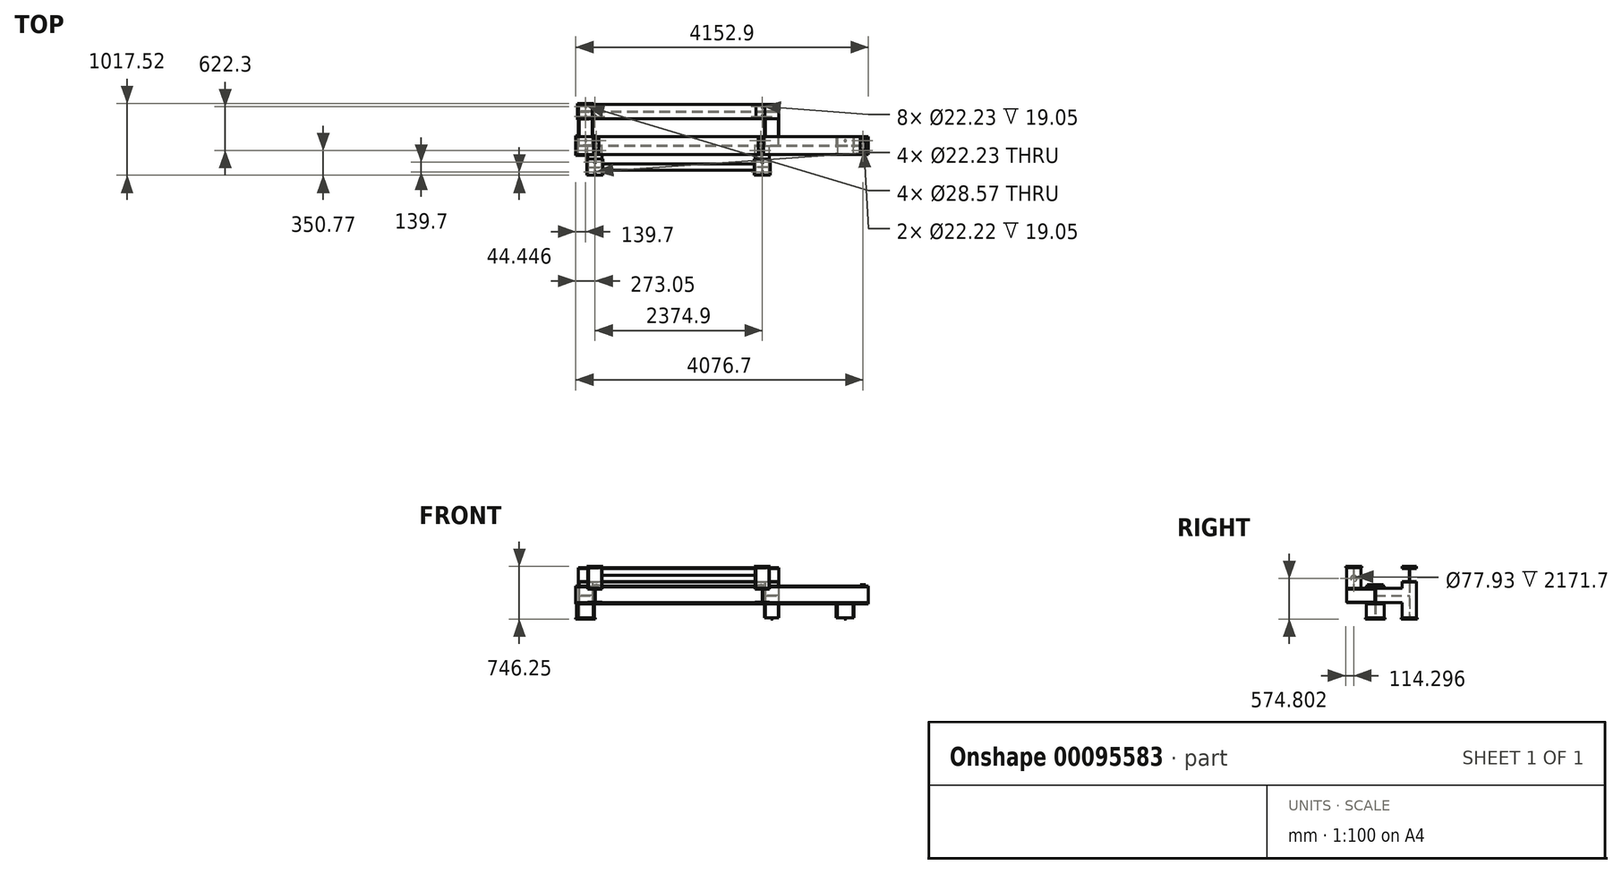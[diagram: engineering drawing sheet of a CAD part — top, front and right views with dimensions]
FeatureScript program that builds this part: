
annotation { "Feature Type Name" : "Feature", "Feature Type Description" : "" }
export const myFeature = defineFeature(function(context is Context, id is Id, definition is map)
    precondition{}
    {
        {
            var Q0;
            Q0=qCreatedBy(makeId("Top.planeOp"),FACE);
            var sketch = newSketch(context, id + "F0", { "sketchPlane" : qUnion([Q0])});
            skLineSegment(sketch, "E0.bottom", {"start": v(-1320.8, 241.3) * mm, "end": v(1320.8, 241.3) * mm, "construction": true});
            skLineSegment(sketch, "E0.top", {"start": v(-1320.8, -241.3) * mm, "end": v(1320.8, -241.3) * mm, "construction": true});
            skLineSegment(sketch, "E0.left", {"start": v(-1320.8, 241.3) * mm, "end": v(-1320.8, -241.3) * mm, "construction": true});
            skLineSegment(sketch, "E0.right", {"start": v(1320.8, 241.3) * mm, "end": v(1320.8, -241.3) * mm, "construction": true});
            skPoint(sketch, "E0.middle", {"position": v(0, 0) * mm});
            skLineSegment(sketch, "E1.bottom", {"start": v(-1435.1, 355.6) * mm, "end": v(-1206.5, 355.6) * mm});
            skLineSegment(sketch, "E1.top", {"start": v(-1435.1, 127) * mm, "end": v(-1206.5, 127) * mm});
            skLineSegment(sketch, "E1.left", {"start": v(-1435.1, 355.6) * mm, "end": v(-1435.1, 127) * mm});
            skLineSegment(sketch, "E1.right", {"start": v(-1206.5, 355.6) * mm, "end": v(-1206.5, 127) * mm});
            skPoint(sketch, "E1.middle", {"position": v(-1320.8, 241.3) * mm});
            skLineSegment(sketch, "E2", {"start": v(0, -413.23) * mm, "end": v(0, 639.03) * mm, "construction": true});
            skLineSegment(sketch, "E3", {"start": v(-1320.8, 355.6) * mm, "end": v(-1320.8, 127) * mm, "construction": true});
            skLineSegment(sketch, "E4", {"start": v(-1435.1, 241.3) * mm, "end": v(-1206.5, 241.3) * mm, "construction": true});
            skLineSegment(sketch, "E5.0", {"start": v(-1435.1, 311.15) * mm, "end": v(-1206.5, 311.15) * mm, "construction": true});
            skCircle(sketch, "E6", {"center": v(-1320.8, 311.15) * mm, "radius": 14.29 * mm});
            skCircle(sketch, "E7.MirrorC", {"center": v(-1320.8, 171.45) * mm, "radius": 14.29 * mm});
            skCircle(sketch, "E8.MirrorC", {"center": v(1320.8, 311.15) * mm, "radius": 14.29 * mm});
            skCircle(sketch, "E9.MirrorC", {"center": v(1320.8, 171.45) * mm, "radius": 14.29 * mm});
            skLineSegment(sketch, "E10.MirrorCS", {"start": v(1435.1, 311.15) * mm, "end": v(1206.5, 311.15) * mm, "construction": true});
            skLineSegment(sketch, "E11.MirrorCS", {"start": v(1435.1, 241.3) * mm, "end": v(1206.5, 241.3) * mm, "construction": true});
            skLineSegment(sketch, "E12.MirrorCS", {"start": v(1320.8, 355.6) * mm, "end": v(1320.8, 127) * mm, "construction": true});
            skLineSegment(sketch, "E13.MirrorCS", {"start": v(1435.1, 355.6) * mm, "end": v(1206.5, 355.6) * mm});
            skPoint(sketch, "E14.MirrorP", {"position": v(1320.8, 241.3) * mm});
            skLineSegment(sketch, "E15.MirrorCS", {"start": v(1206.5, 355.6) * mm, "end": v(1206.5, 127) * mm});
            skLineSegment(sketch, "E16.MirrorCS", {"start": v(1435.1, 127) * mm, "end": v(1206.5, 127) * mm});
            skLineSegment(sketch, "E17.MirrorCS", {"start": v(1435.1, 355.6) * mm, "end": v(1435.1, 127) * mm});
            skLineSegment(sketch, "E18.bottom", {"start": v(-1460.5, -381) * mm, "end": v(-1181.1, -381) * mm});
            skLineSegment(sketch, "E18.top", {"start": v(-1460.5, -101.6) * mm, "end": v(-1181.1, -101.6) * mm});
            skLineSegment(sketch, "E18.left", {"start": v(-1460.5, -381) * mm, "end": v(-1460.5, -101.6) * mm});
            skLineSegment(sketch, "E18.right", {"start": v(-1181.1, -381) * mm, "end": v(-1181.1, -101.6) * mm});
            skPoint(sketch, "E18.middle", {"position": v(-1320.8, -241.3) * mm});
            skLineSegment(sketch, "E19", {"start": v(-1320.8, -241.3) * mm, "end": v(-1460.5, -241.3) * mm, "construction": true});
            skLineSegment(sketch, "E20.0", {"start": v(-1320.8, -171.45) * mm, "end": v(-1460.5, -171.45) * mm, "construction": true});
            skCircle(sketch, "E21", {"center": v(-1320.8, -171.45) * mm, "radius": 14.29 * mm});
            skCircle(sketch, "E22.MirrorC", {"center": v(-1320.8, -311.15) * mm, "radius": 14.29 * mm});
            skLineSegment(sketch, "E23", {"start": v(-1320.8, -638.8) * mm, "end": v(-1320.8, -1011) * mm, "construction": true});
            skPoint(sketch, "E24.orphan", {"position": v(-1320.8, -381) * mm});
            skLineSegment(sketch, "E25.0", {"start": v(0, -638.8) * mm, "end": v(0, -1011) * mm, "construction": true});
            skLineSegment(sketch, "E26.0", {"start": v(1320.8, -638.8) * mm, "end": v(1320.8, -1011) * mm, "construction": true});
            skLineSegment(sketch, "E27.0", {"start": v(2362.2, -638.8) * mm, "end": v(2362.2, -1011) * mm, "construction": true});
            skLineSegment(sketch, "E28", {"start": v(-1320.8, -1011) * mm, "end": v(2362.2, -1011) * mm, "construction": true});
            skLineSegment(sketch, "E29", {"start": v(520.7, -1011) * mm, "end": v(520.7, -1354.57) * mm, "construction": true});
            skCircle(sketch, "E30.MirrorC", {"center": v(2362.2, -171.45) * mm, "radius": 14.29 * mm});
            skCircle(sketch, "E31.MirrorC", {"center": v(2362.2, -311.15) * mm, "radius": 14.29 * mm});
            skLineSegment(sketch, "E32.MirrorCS", {"start": v(2362.2, -171.45) * mm, "end": v(2501.9, -171.45) * mm, "construction": true});
            skLineSegment(sketch, "E33.MirrorCS", {"start": v(2501.9, -101.6) * mm, "end": v(2222.5, -101.6) * mm});
            skLineSegment(sketch, "E34.MirrorCS", {"start": v(2501.9, -381) * mm, "end": v(2222.5, -381) * mm});
            skLineSegment(sketch, "E35.MirrorCS", {"start": v(2362.2, -241.3) * mm, "end": v(2501.9, -241.3) * mm, "construction": true});
            skPoint(sketch, "E36.MirrorP", {"position": v(2362.2, -241.3) * mm});
            skLineSegment(sketch, "E37.MirrorCS", {"start": v(2222.5, -381) * mm, "end": v(2222.5, -101.6) * mm});
            skPoint(sketch, "E38.MirrorP", {"position": v(2362.2, -381) * mm});
            skLineSegment(sketch, "E39.MirrorCS", {"start": v(2501.9, -381) * mm, "end": v(2501.9, -101.6) * mm});
            skSolve(sketch);
        }
        {
            var Q0;
            Q0=makeQuery(id+"F0.imprint","IMPRINT",FACE,{"disambiguationData":[TD([[makeQuery(id+"F0.imprint","IMPRINT",EDGE,{"derivedFrom":sQuery(id+"F0.wireOp",EDGE,"E1.bottom")}),-1.0]])]});
            var Q1;
            Q1=makeQuery(id+"F0.imprint","IMPRINT",FACE,{"disambiguationData":[TD([[makeQuery(id+"F0.imprint","IMPRINT",EDGE,{"derivedFrom":sQuery(id+"F0.wireOp",EDGE,"E8.MirrorC")}),1.0]])]});
            var Q2;
            Q2=makeQuery(id+"F0.imprint","IMPRINT",FACE,{"disambiguationData":[TD([[makeQuery(id+"F0.imprint","IMPRINT",EDGE,{"derivedFrom":sQuery(id+"F0.wireOp",EDGE,"E30.MirrorC")}),1.0]])]});
            var Q3;
            Q3=makeQuery(id+"F0.imprint","IMPRINT",FACE,{"disambiguationData":[TD([[makeQuery(id+"F0.imprint","IMPRINT",EDGE,{"derivedFrom":sQuery(id+"F0.wireOp",EDGE,"E18.bottom")}),1.0]])]});
            extrude(context, id + "F1", {"entities" : qUnion([Q0, Q1, Q2, Q3]), "depth" : 19.05 * mm});
        }
        {
            var Q0;
            Q0=makeQuery(id+"F1.opExtrude","CAP_FACE",FACE,{"disambiguationData":[OSD([sQuery(id+"F0.wireOp",EDGE,"E1.bottom"),sQuery(id+"F0.wireOp",EDGE,"E1.top"),sQuery(id+"F0.wireOp",EDGE,"E1.left"),sQuery(id+"F0.wireOp",EDGE,"E1.right"),sQuery(id+"F0.wireOp",EDGE,"E6"),sQuery(id+"F0.wireOp",EDGE,"E7.MirrorC")])],"isStart":false});
            var sketch = newSketch(context, id + "F2", { "sketchPlane" : qUnion([Q0])});
            skLineSegment(sketch, "E40.0", {"start": v(-1435.1, 241.3) * mm, "end": v(-1206.5, 241.3) * mm, "construction": true});
            skLineSegment(sketch, "E41.0", {"start": v(-1320.8, 355.6) * mm, "end": v(-1320.8, 127) * mm, "construction": true});
            skLineSegment(sketch, "E42.bottom", {"start": v(-1422.4, 342.9) * mm, "end": v(-1411.35, 342.9) * mm});
            skLineSegment(sketch, "E42.top", {"start": v(-1422.4, 139.7) * mm, "end": v(-1411.35, 139.7) * mm});
            skLineSegment(sketch, "E42.left", {"start": v(-1422.4, 342.9) * mm, "end": v(-1422.4, 139.7) * mm});
            skLineSegment(sketch, "E42.right", {"start": v(-1219.2, 342.9) * mm, "end": v(-1219.2, 139.7) * mm, "construction": true});
            skPoint(sketch, "E42.middle", {"position": v(-1320.8, 241.3) * mm});
            skLineSegment(sketch, "E43.0", {"start": v(-1411.35, 342.9) * mm, "end": v(-1411.35, 251.27) * mm});
            skLineSegment(sketch, "E44.trimOffspring", {"start": v(-1405, 237.68) * mm, "end": v(-1320.8, 237.68) * mm});
            skLineSegment(sketch, "E45.MirrorCS", {"start": v(-1405, 244.92) * mm, "end": v(-1320.8, 244.92) * mm});
            skLineSegment(sketch, "E46.trimOffspring", {"start": v(-1411.35, 231.33) * mm, "end": v(-1411.35, 139.7) * mm});
            skPoint(sketch, "E47.visualSharp", {"position": v(-1411.35, 244.92) * mm});
            skArc(sketch, "E47.filletArc", {"start": v(-1411.35, 251.27) * mm, "mid": v(-1409.5, 246.78) * mm, "end": v(-1405, 244.92) * mm});
            skPoint(sketch, "E48.visualSharp", {"position": v(-1411.35, 237.68) * mm});
            skArc(sketch, "E48.filletArc", {"start": v(-1405, 237.68) * mm, "mid": v(-1409.5, 235.82) * mm, "end": v(-1411.35, 231.33) * mm});
            skArc(sketch, "E49.MirrorCS", {"start": v(-1236.6, 237.68) * mm, "mid": v(-1232.1, 235.82) * mm, "end": v(-1230.25, 231.33) * mm});
            skArc(sketch, "E50.MirrorCS", {"start": v(-1230.25, 251.27) * mm, "mid": v(-1232.1, 246.78) * mm, "end": v(-1236.6, 244.92) * mm});
            skPoint(sketch, "E51.MirrorP", {"position": v(-1230.25, 237.68) * mm});
            skPoint(sketch, "E52.MirrorP", {"position": v(-1230.25, 244.92) * mm});
            skLineSegment(sketch, "E53.MirrorCS", {"start": v(-1230.25, 342.9) * mm, "end": v(-1230.25, 251.27) * mm});
            skLineSegment(sketch, "E54.MirrorCS", {"start": v(-1236.6, 237.68) * mm, "end": v(-1320.8, 237.68) * mm});
            skLineSegment(sketch, "E55.MirrorCS", {"start": v(-1236.6, 244.92) * mm, "end": v(-1320.8, 244.92) * mm});
            skLineSegment(sketch, "E56.MirrorCS", {"start": v(-1219.2, 139.7) * mm, "end": v(-1230.25, 139.7) * mm});
            skLineSegment(sketch, "E57.MirrorCS", {"start": v(-1230.25, 231.33) * mm, "end": v(-1230.25, 139.7) * mm});
            skLineSegment(sketch, "E58.MirrorCS", {"start": v(-1219.2, 342.9) * mm, "end": v(-1230.25, 342.9) * mm});
            skLineSegment(sketch, "E59.MirrorCS", {"start": v(-1219.2, 342.9) * mm, "end": v(-1219.2, 139.7) * mm});
            skLineSegment(sketch, "E60.0", {"start": v(0, -413.23) * mm, "end": v(0, 639.03) * mm, "construction": true});
            skArc(sketch, "E61.MirrorCS", {"start": v(1411.35, 251.27) * mm, "mid": v(1409.5, 246.78) * mm, "end": v(1405, 244.92) * mm});
            skArc(sketch, "E62.MirrorCS", {"start": v(1405, 237.68) * mm, "mid": v(1409.5, 235.82) * mm, "end": v(1411.35, 231.33) * mm});
            skLineSegment(sketch, "E63.MirrorCS", {"start": v(1236.6, 244.92) * mm, "end": v(1320.8, 244.92) * mm});
            skArc(sketch, "E64.MirrorCS", {"start": v(1236.6, 237.68) * mm, "mid": v(1232.1, 235.82) * mm, "end": v(1230.25, 231.33) * mm});
            skLineSegment(sketch, "E65.MirrorCS", {"start": v(1422.4, 139.7) * mm, "end": v(1411.35, 139.7) * mm});
            skLineSegment(sketch, "E66.MirrorCS", {"start": v(1422.4, 342.9) * mm, "end": v(1411.35, 342.9) * mm});
            skArc(sketch, "E67.MirrorCS", {"start": v(1230.25, 251.27) * mm, "mid": v(1232.1, 246.78) * mm, "end": v(1236.6, 244.92) * mm});
            skLineSegment(sketch, "E68.MirrorCS", {"start": v(1236.6, 237.68) * mm, "end": v(1320.8, 237.68) * mm});
            skLineSegment(sketch, "E69.MirrorCS", {"start": v(1435.1, 241.3) * mm, "end": v(1206.5, 241.3) * mm, "construction": true});
            skLineSegment(sketch, "E70.MirrorCS", {"start": v(1405, 237.68) * mm, "end": v(1320.8, 237.68) * mm});
            skLineSegment(sketch, "E71.MirrorCS", {"start": v(1219.2, 342.9) * mm, "end": v(1230.25, 342.9) * mm});
            skLineSegment(sketch, "E72.MirrorCS", {"start": v(1219.2, 139.7) * mm, "end": v(1230.25, 139.7) * mm});
            skLineSegment(sketch, "E73.MirrorCS", {"start": v(1411.35, 342.9) * mm, "end": v(1411.35, 251.27) * mm});
            skLineSegment(sketch, "E74.MirrorCS", {"start": v(1405, 244.92) * mm, "end": v(1320.8, 244.92) * mm});
            skLineSegment(sketch, "E75.MirrorCS", {"start": v(1411.35, 231.33) * mm, "end": v(1411.35, 139.7) * mm});
            skPoint(sketch, "E76.MirrorP", {"position": v(1411.35, 237.68) * mm});
            skPoint(sketch, "E77.MirrorP", {"position": v(1320.8, 241.3) * mm});
            skLineSegment(sketch, "E78.MirrorCS", {"start": v(1219.2, 342.9) * mm, "end": v(1219.2, 139.7) * mm, "construction": true});
            skLineSegment(sketch, "E79.MirrorCS", {"start": v(1422.4, 342.9) * mm, "end": v(1422.4, 139.7) * mm});
            skPoint(sketch, "E80.MirrorP", {"position": v(1230.25, 237.68) * mm});
            skLineSegment(sketch, "E81.MirrorCS", {"start": v(1320.8, 355.6) * mm, "end": v(1320.8, 127) * mm, "construction": true});
            skPoint(sketch, "E82.MirrorP", {"position": v(1411.35, 244.92) * mm});
            skLineSegment(sketch, "E83.MirrorCS", {"start": v(1219.2, 342.9) * mm, "end": v(1219.2, 139.7) * mm});
            skLineSegment(sketch, "E84.MirrorCS", {"start": v(1230.25, 231.33) * mm, "end": v(1230.25, 139.7) * mm});
            skLineSegment(sketch, "E85.MirrorCS", {"start": v(1230.25, 342.9) * mm, "end": v(1230.25, 251.27) * mm});
            skPoint(sketch, "E86.MirrorP", {"position": v(1230.25, 244.92) * mm});
            skSolve(sketch);
        }
        {
            var Q0;
            Q0 = qSketchRegion(id + "F2", true);
            extrude(context, id + "F3", {"entities" : qUnion([Q0]), "depth" : 504.95 * mm});
        }
        {
            var Q0;
            Q0=makeQuery(id+"F3.opExtrude","SWEPT_FACE",FACE,{"disambiguationData":[OSD([sQuery(id+"F2.wireOp",EDGE,"E79.MirrorCS")])]});
            var sketch = newSketch(context, id + "F4", { "sketchPlane" : qUnion([Q0])});
            skLineSegment(sketch, "E87.bottom", {"start": v(139.7, 524) * mm, "end": v(342.9, 524) * mm});
            skLineSegment(sketch, "E87.top", {"start": v(139.7, 727.2) * mm, "end": v(342.9, 727.2) * mm});
            skLineSegment(sketch, "E87.left", {"start": v(139.7, 524) * mm, "end": v(139.7, 535.05) * mm});
            skLineSegment(sketch, "E87.right", {"start": v(342.9, 524) * mm, "end": v(342.9, 535.05) * mm});
            skLineSegment(sketch, "E88", {"start": v(241.3, 727.2) * mm, "end": v(241.3, 524) * mm, "construction": true});
            skLineSegment(sketch, "E89.0", {"start": v(237.68, 709.8) * mm, "end": v(237.68, 541.4) * mm});
            skLineSegment(sketch, "E90.MirrorCS", {"start": v(244.92, 709.8) * mm, "end": v(244.92, 541.4) * mm});
            skLineSegment(sketch, "E91.0", {"start": v(139.7, 716.15) * mm, "end": v(231.33, 716.15) * mm});
            skLineSegment(sketch, "E92.0", {"start": v(139.7, 535.05) * mm, "end": v(231.33, 535.05) * mm});
            skLineSegment(sketch, "E93.trimOffspring", {"start": v(251.27, 716.15) * mm, "end": v(342.9, 716.15) * mm});
            skLineSegment(sketch, "E94.trimOffspring", {"start": v(251.27, 535.05) * mm, "end": v(342.9, 535.05) * mm});
            skLineSegment(sketch, "E95.trimOffspring", {"start": v(139.7, 716.15) * mm, "end": v(139.7, 727.2) * mm});
            skLineSegment(sketch, "E96.trimOffspring", {"start": v(342.9, 716.15) * mm, "end": v(342.9, 727.2) * mm});
            skPoint(sketch, "E97.newPointB", {"position": v(237.68, 524) * mm});
            skArc(sketch, "E97.filletArc", {"start": v(231.33, 535.05) * mm, "mid": v(235.82, 536.91) * mm, "end": v(237.68, 541.4) * mm});
            skPoint(sketch, "E98.newPointA", {"position": v(244.92, 524) * mm});
            skArc(sketch, "E98.filletArc", {"start": v(244.92, 541.4) * mm, "mid": v(246.78, 536.91) * mm, "end": v(251.27, 535.05) * mm});
            skPoint(sketch, "E99.newPointA", {"position": v(237.68, 727.2) * mm});
            skArc(sketch, "E99.filletArc", {"start": v(237.68, 709.8) * mm, "mid": v(235.82, 714.3) * mm, "end": v(231.33, 716.15) * mm});
            skPoint(sketch, "E100.newPointA", {"position": v(244.92, 727.2) * mm});
            skArc(sketch, "E100.filletArc", {"start": v(251.27, 716.15) * mm, "mid": v(246.78, 714.3) * mm, "end": v(244.92, 709.8) * mm});
            skSolve(sketch);
        }
        {
            var Q0;
            Q0 = qSketchRegion(id + "F4", true);
            var Q1;
            Q1=makeQuery(id+"F3.opExtrude","SWEPT_FACE",FACE,{"disambiguationData":[OSD([sQuery(id+"F2.wireOp",EDGE,"E42.left")])]});
            extrude(context, id + "F5", {"entities" : qUnion([Q0]), "endBound" : BoundingType.UP_TO_SURFACE, "oppositeDirection" : true, "endBoundEntityFace" : qUnion([Q1]), "depth" : 25.4 * mm});
        }
        {
            var Q0;
            Q0=makeQuery(id+"F5.opExtrude","SWEPT_FACE",FACE,{"disambiguationData":[OSD([sQuery(id+"F4.wireOp",EDGE,"E87.top")])]});
            var sketch = newSketch(context, id + "F6", { "sketchPlane" : qUnion([Q0])});
            skLineSegment(sketch, "E101.0", {"start": v(0, -413.23) * mm, "end": v(0, 639.03) * mm, "construction": true});
            skLineSegment(sketch, "E102.0", {"start": v(-1187.45, -413.23) * mm, "end": v(-1187.45, 639.03) * mm, "construction": true});
            skLineSegment(sketch, "E103.0", {"start": v(-1225.55, 139.7) * mm, "end": v(-1225.55, 342.9) * mm});
            skLineSegment(sketch, "E104.0", {"start": v(-1098.55, 139.7) * mm, "end": v(-1098.55, 342.9) * mm});
            skLineSegment(sketch, "E105.0", {"start": v(-1422.4, 342.9) * mm, "end": v(1422.4, 342.9) * mm, "construction": true});
            skLineSegment(sketch, "E106.0.0", {"start": v(1225.55, 342.9) * mm, "end": v(-1225.55, 342.9) * mm});
            skLineSegment(sketch, "E106.0.1", {"start": v(-1422.4, 342.9) * mm, "end": v(-1422.4, 139.7) * mm});
            skLineSegment(sketch, "E106.0.2", {"start": v(-1225.55, 139.7) * mm, "end": v(-1098.55, 139.7) * mm});
            skLineSegment(sketch, "E106.0.3", {"start": v(1422.4, 139.7) * mm, "end": v(1422.4, 342.9) * mm});
            skLineSegment(sketch, "E107.trimOffspring", {"start": v(0, 139.7) * mm, "end": v(1225.55, 139.7) * mm});
            skLineSegment(sketch, "E108.0", {"start": v(-1320.8, 241.3) * mm, "end": v(1320.8, 241.3) * mm, "construction": true});
            skLineSegment(sketch, "E109.0", {"start": v(-1320.8, 311.15) * mm, "end": v(1320.8, 311.15) * mm, "construction": true});
            skCircle(sketch, "E110", {"center": v(-1187.45, 311.15) * mm, "radius": 11.11 * mm});
            skCircle(sketch, "E111.MirrorC", {"center": v(-1187.45, 171.45) * mm, "radius": 11.11 * mm});
            skCircle(sketch, "E112.MirrorC", {"center": v(1187.45, 311.15) * mm, "radius": 11.11 * mm});
            skCircle(sketch, "E113.MirrorC", {"center": v(1187.45, 171.45) * mm, "radius": 11.11 * mm});
            skLineSegment(sketch, "E114.MirrorCS", {"start": v(1225.55, 139.7) * mm, "end": v(1098.55, 139.7) * mm});
            skLineSegment(sketch, "E115.MirrorCS", {"start": v(1225.55, 139.7) * mm, "end": v(1225.55, 342.9) * mm});
            skLineSegment(sketch, "E116.MirrorCS", {"start": v(1098.55, 139.7) * mm, "end": v(1098.55, 342.9) * mm});
            skSolve(sketch);
        }
        {
            var Q0;
            Q0 = qSketchRegion(id + "F6", true);
            extrude(context, id + "F7", {"entities" : qUnion([Q0]), "operationType" : NewBodyOperationType.ADD, "depth" : 19.05 * mm});
        }
        {
            var Q0;
            Q0=makeQuery(id+"F3.opExtrude","SWEPT_FACE",FACE,{"disambiguationData":[OSD([sQuery(id+"F2.wireOp",EDGE,"E44.trimOffspring"),sQuery(id+"F2.wireOp",EDGE,"E54.MirrorCS")])]});
            var sketch = newSketch(context, id + "F8", { "sketchPlane" : qUnion([Q0])});
            skLineSegment(sketch, "E117.0", {"start": v(-1460.5, 0) * mm, "end": v(-1181.1, 0) * mm, "construction": true});
            skLineSegment(sketch, "E118", {"start": v(-1320.8, 0) * mm, "end": v(-1320.8, 868.41) * mm, "construction": true});
            skLineSegment(sketch, "E119.0", {"start": v(-1422.4, 231.65) * mm, "end": v(-1411.35, 231.65) * mm});
            skLineSegment(sketch, "E120.0", {"start": v(-1422.4, 434.85) * mm, "end": v(-1411.35, 434.85) * mm});
            skLineSegment(sketch, "E121", {"start": v(-1422.4, 434.85) * mm, "end": v(-1422.4, 231.65) * mm});
            skLineSegment(sketch, "E122.0", {"start": v(-1411.35, 434.85) * mm, "end": v(-1411.35, 342.77) * mm});
            skLineSegment(sketch, "E123", {"start": v(-1411.35, 333.25) * mm, "end": v(-1320.8, 333.25) * mm, "construction": true});
            skLineSegment(sketch, "E124.0", {"start": v(-1405, 336.42) * mm, "end": v(-1320.8, 336.42) * mm});
            skLineSegment(sketch, "E125.MirrorCS", {"start": v(-1410.08, 330.07) * mm, "end": v(-1320.8, 330.07) * mm});
            skLineSegment(sketch, "E126.trimOffspring", {"start": v(-1411.35, 328.8) * mm, "end": v(-1411.35, 231.65) * mm});
            skPoint(sketch, "E127.newPointA", {"position": v(-1411.35, 336.42) * mm});
            skArc(sketch, "E127.filletArc", {"start": v(-1411.35, 342.77) * mm, "mid": v(-1409.5, 338.28) * mm, "end": v(-1405, 336.42) * mm});
            skPoint(sketch, "E128.visualSharp", {"position": v(-1411.35, 330.07) * mm});
            skArc(sketch, "E128.filletArc", {"start": v(-1410.08, 330.07) * mm, "mid": v(-1410.98, 329.7) * mm, "end": v(-1411.35, 328.8) * mm});
            skArc(sketch, "E129.MirrorCS", {"start": v(-1231.52, 330.07) * mm, "mid": v(-1230.62, 329.7) * mm, "end": v(-1230.25, 328.8) * mm});
            skArc(sketch, "E130.MirrorCS", {"start": v(-1230.25, 342.77) * mm, "mid": v(-1232.1, 338.28) * mm, "end": v(-1236.6, 336.42) * mm});
            skLineSegment(sketch, "E131.MirrorCS", {"start": v(-1219.2, 231.65) * mm, "end": v(-1230.25, 231.65) * mm});
            skLineSegment(sketch, "E132.MirrorCS", {"start": v(-1219.2, 434.85) * mm, "end": v(-1230.25, 434.85) * mm});
            skPoint(sketch, "E133.MirrorP", {"position": v(-1230.25, 336.42) * mm});
            skPoint(sketch, "E134.MirrorP", {"position": v(-1230.25, 330.07) * mm});
            skLineSegment(sketch, "E135.MirrorCS", {"start": v(-1230.25, 328.8) * mm, "end": v(-1230.25, 231.65) * mm});
            skLineSegment(sketch, "E136.MirrorCS", {"start": v(-1231.52, 330.07) * mm, "end": v(-1320.8, 330.07) * mm});
            skLineSegment(sketch, "E137.MirrorCS", {"start": v(-1219.2, 434.85) * mm, "end": v(-1219.2, 231.65) * mm});
            skLineSegment(sketch, "E138.MirrorCS", {"start": v(-1230.25, 434.85) * mm, "end": v(-1230.25, 342.77) * mm});
            skLineSegment(sketch, "E139.MirrorCS", {"start": v(-1230.25, 333.25) * mm, "end": v(-1320.8, 333.25) * mm, "construction": true});
            skLineSegment(sketch, "E140.MirrorCS", {"start": v(-1236.6, 336.42) * mm, "end": v(-1320.8, 336.42) * mm});
            skLineSegment(sketch, "E141", {"start": v(0, -179.83) * mm, "end": v(0, 965.66) * mm, "construction": true});
            skArc(sketch, "E142.MirrorCS", {"start": v(1411.35, 342.77) * mm, "mid": v(1409.5, 338.28) * mm, "end": v(1405, 336.42) * mm});
            skArc(sketch, "E143.MirrorCS", {"start": v(1410.08, 330.07) * mm, "mid": v(1410.98, 329.7) * mm, "end": v(1411.35, 328.8) * mm});
            skArc(sketch, "E144.MirrorCS", {"start": v(1230.25, 342.77) * mm, "mid": v(1232.1, 338.28) * mm, "end": v(1236.6, 336.42) * mm});
            skArc(sketch, "E145.MirrorCS", {"start": v(1231.52, 330.07) * mm, "mid": v(1230.62, 329.7) * mm, "end": v(1230.25, 328.8) * mm});
            skLineSegment(sketch, "E146.MirrorCS", {"start": v(1411.35, 333.25) * mm, "end": v(1320.8, 333.25) * mm, "construction": true});
            skLineSegment(sketch, "E147.MirrorCS", {"start": v(1219.2, 231.65) * mm, "end": v(1230.25, 231.65) * mm});
            skLineSegment(sketch, "E148.MirrorCS", {"start": v(1219.2, 434.85) * mm, "end": v(1230.25, 434.85) * mm});
            skLineSegment(sketch, "E149.MirrorCS", {"start": v(1422.4, 231.65) * mm, "end": v(1411.35, 231.65) * mm});
            skLineSegment(sketch, "E150.MirrorCS", {"start": v(1422.4, 434.85) * mm, "end": v(1411.35, 434.85) * mm});
            skLineSegment(sketch, "E151.MirrorCS", {"start": v(1405, 336.42) * mm, "end": v(1320.8, 336.42) * mm});
            skLineSegment(sketch, "E152.MirrorCS", {"start": v(1410.08, 330.07) * mm, "end": v(1320.8, 330.07) * mm});
            skLineSegment(sketch, "E153.MirrorCS", {"start": v(1230.25, 333.25) * mm, "end": v(1320.8, 333.25) * mm, "construction": true});
            skLineSegment(sketch, "E154.MirrorCS", {"start": v(1231.52, 330.07) * mm, "end": v(1320.8, 330.07) * mm});
            skLineSegment(sketch, "E155.MirrorCS", {"start": v(1236.6, 336.42) * mm, "end": v(1320.8, 336.42) * mm});
            skLineSegment(sketch, "E156.MirrorCS", {"start": v(1411.35, 328.8) * mm, "end": v(1411.35, 231.65) * mm});
            skPoint(sketch, "E157.MirrorP", {"position": v(1411.35, 330.07) * mm});
            skPoint(sketch, "E158.MirrorP", {"position": v(1411.35, 336.42) * mm});
            skLineSegment(sketch, "E159.MirrorCS", {"start": v(1422.4, 434.85) * mm, "end": v(1422.4, 231.65) * mm});
            skLineSegment(sketch, "E160.MirrorCS", {"start": v(1411.35, 434.85) * mm, "end": v(1411.35, 342.77) * mm});
            skLineSegment(sketch, "E161.MirrorCS", {"start": v(1230.25, 434.85) * mm, "end": v(1230.25, 342.77) * mm});
            skLineSegment(sketch, "E162.MirrorCS", {"start": v(1230.25, 328.8) * mm, "end": v(1230.25, 231.65) * mm});
            skPoint(sketch, "E163.MirrorP", {"position": v(1230.25, 330.07) * mm});
            skPoint(sketch, "E164.MirrorP", {"position": v(1230.25, 336.42) * mm});
            skLineSegment(sketch, "E165.MirrorCS", {"start": v(1219.2, 434.85) * mm, "end": v(1219.2, 231.65) * mm});
            skSolve(sketch);
        }
        {
            var Q0;
            Q0 = qSketchRegion(id + "F8", true);
            extrude(context, id + "F9", {"entities" : qUnion([Q0]), "operationType" : NewBodyOperationType.ADD, "depth" : 482.6 * mm});
        }
        {
            var Q0;
            Q0=qCreatedBy(makeId("Right.planeOp"),FACE);
            cPlane(context, id + "F10", {"entities" : qUnion([Q0]), "cplaneType" : CPlaneType.OFFSET, "offset" : 2692.4 * mm, "width" : 152.4 * mm, "height" : 152.4 * mm});
        }
        {
            var Q0;
            Q0=qCreatedBy(id+"F10.planeOp",FACE);
            var sketch = newSketch(context, id + "F11", { "sketchPlane" : qUnion([Q0])});
            skLineSegment(sketch, "E166.0", {"start": v(-381, 19.05) * mm, "end": v(-101.6, 19.05) * mm, "construction": true});
            skLineSegment(sketch, "E167", {"start": v(-241.3, 19.05) * mm, "end": v(-241.3, 468.37) * mm, "construction": true});
            skLineSegment(sketch, "E168.0", {"start": v(-381, 217.42) * mm, "end": v(-101.6, 217.42) * mm, "construction": true});
            skLineSegment(sketch, "E169.bottom", {"start": v(-368.3, 217.42) * mm, "end": v(-114.3, 217.42) * mm});
            skLineSegment(sketch, "E169.top", {"start": v(-368.3, 471.42) * mm, "end": v(-114.3, 471.42) * mm});
            skLineSegment(sketch, "E169.left", {"start": v(-368.3, 217.42) * mm, "end": v(-368.3, 231.65) * mm});
            skLineSegment(sketch, "E169.right", {"start": v(-114.3, 217.42) * mm, "end": v(-114.3, 231.65) * mm});
            skLineSegment(sketch, "E170.0", {"start": v(-368.3, 457.2) * mm, "end": v(-254, 457.2) * mm});
            skLineSegment(sketch, "E171.0", {"start": v(-368.3, 231.65) * mm, "end": v(-254, 231.65) * mm});
            skLineSegment(sketch, "E172.0", {"start": v(-234.95, 238) * mm, "end": v(-234.95, 450.85) * mm});
            skLineSegment(sketch, "E173.MirrorCS", {"start": v(-247.65, 238) * mm, "end": v(-247.65, 450.85) * mm});
            skLineSegment(sketch, "E174.trimOffspring", {"start": v(-368.3, 457.2) * mm, "end": v(-368.3, 471.42) * mm});
            skLineSegment(sketch, "E175.trimOffspring", {"start": v(-114.3, 457.2) * mm, "end": v(-114.3, 471.42) * mm});
            skLineSegment(sketch, "E176.trimOffspring", {"start": v(-228.6, 457.2) * mm, "end": v(-114.3, 457.2) * mm});
            skLineSegment(sketch, "E177.trimOffspring", {"start": v(-228.6, 231.65) * mm, "end": v(-114.3, 231.65) * mm});
            skPoint(sketch, "E178.newPointB", {"position": v(-247.65, 468.37) * mm});
            skArc(sketch, "E178.filletArc", {"start": v(-247.65, 450.85) * mm, "mid": v(-249.5, 455.34) * mm, "end": v(-254, 457.2) * mm});
            skPoint(sketch, "E179.newPointB", {"position": v(-234.95, 468.37) * mm});
            skArc(sketch, "E179.filletArc", {"start": v(-228.6, 457.2) * mm, "mid": v(-233.1, 455.34) * mm, "end": v(-234.95, 450.85) * mm});
            skPoint(sketch, "E180.newPointB", {"position": v(-234.95, 19.05) * mm});
            skArc(sketch, "E180.filletArc", {"start": v(-234.95, 238) * mm, "mid": v(-233.1, 233.5) * mm, "end": v(-228.6, 231.65) * mm});
            skPoint(sketch, "E181.newPointA", {"position": v(-247.65, 19.05) * mm});
            skArc(sketch, "E181.filletArc", {"start": v(-254, 231.65) * mm, "mid": v(-249.5, 233.5) * mm, "end": v(-247.65, 238) * mm});
            skSolve(sketch);
        }
        {
            var Q0;
            Q0 = qSketchRegion(id + "F11", true);
            extrude(context, id + "F12", {"entities" : qUnion([Q0]), "oppositeDirection" : true, "depth" : 4152.9 * mm});
        }
        {
            var Q0;
            Q0=makeQuery(id+"F1.opExtrude","CAP_FACE",FACE,{"disambiguationData":[OSD([sQuery(id+"F0.wireOp",EDGE,"E18.bottom"),sQuery(id+"F0.wireOp",EDGE,"E18.top"),sQuery(id+"F0.wireOp",EDGE,"E18.left"),sQuery(id+"F0.wireOp",EDGE,"E18.right"),sQuery(id+"F0.wireOp",EDGE,"E21"),sQuery(id+"F0.wireOp",EDGE,"E22.MirrorC")])],"isStart":false});
            var sketch = newSketch(context, id + "F13", { "sketchPlane" : qUnion([Q0])});
            skLineSegment(sketch, "E182.bottom", {"start": v(-1447.8, -114.3) * mm, "end": v(-1433.58, -114.3) * mm});
            skLineSegment(sketch, "E182.top", {"start": v(-1447.8, -368.3) * mm, "end": v(-1433.58, -368.3) * mm});
            skLineSegment(sketch, "E182.left", {"start": v(-1447.8, -114.3) * mm, "end": v(-1447.8, -368.3) * mm});
            skLineSegment(sketch, "E182.right", {"start": v(-1193.8, -114.3) * mm, "end": v(-1193.8, -368.3) * mm});
            skPoint(sketch, "E182.middle", {"position": v(-1320.8, -241.3) * mm});
            skLineSegment(sketch, "E183.0", {"start": v(-1433.58, -114.3) * mm, "end": v(-1433.58, -236.98) * mm});
            skLineSegment(sketch, "E184.0", {"start": v(-1208.02, -114.3) * mm, "end": v(-1208.02, -236.98) * mm});
            skLineSegment(sketch, "E185.trimOffspring", {"start": v(-1208.02, -114.3) * mm, "end": v(-1193.8, -114.3) * mm});
            skLineSegment(sketch, "E186.trimOffspring", {"start": v(-1208.02, -368.3) * mm, "end": v(-1193.8, -368.3) * mm});
            skLineSegment(sketch, "E187.0", {"start": v(-1208.02, -236.98) * mm, "end": v(-1433.58, -236.98) * mm});
            skLineSegment(sketch, "E188.MirrorCS", {"start": v(-1208.02, -245.62) * mm, "end": v(-1433.58, -245.62) * mm});
            skPoint(sketch, "E189.orphan", {"position": v(-1460.5, -236.98) * mm});
            skPoint(sketch, "E190.orphan", {"position": v(-1460.5, -245.62) * mm});
            skLineSegment(sketch, "E191.trimOffspring", {"start": v(-1433.58, -245.62) * mm, "end": v(-1433.58, -368.3) * mm});
            skPoint(sketch, "E192.orphan", {"position": v(-1320.8, -236.98) * mm});
            skPoint(sketch, "E193.orphan", {"position": v(-1320.8, -245.62) * mm});
            skLineSegment(sketch, "E194.trimOffspring", {"start": v(-1208.02, -245.62) * mm, "end": v(-1208.02, -368.3) * mm});
            skLineSegment(sketch, "E195.MirrorCS", {"start": v(2489.2, -368.3) * mm, "end": v(2474.98, -368.3) * mm});
            skLineSegment(sketch, "E196.MirrorCS", {"start": v(2489.2, -114.3) * mm, "end": v(2474.98, -114.3) * mm});
            skLineSegment(sketch, "E197.MirrorCS", {"start": v(2249.42, -368.3) * mm, "end": v(2235.2, -368.3) * mm});
            skLineSegment(sketch, "E198.MirrorCS", {"start": v(2249.42, -114.3) * mm, "end": v(2235.2, -114.3) * mm});
            skPoint(sketch, "E199.MirrorP", {"position": v(2362.2, -245.62) * mm});
            skPoint(sketch, "E200.MirrorP", {"position": v(2362.2, -236.98) * mm});
            skLineSegment(sketch, "E201.MirrorCS", {"start": v(2249.42, -245.62) * mm, "end": v(2474.98, -245.62) * mm});
            skPoint(sketch, "E202.MirrorP", {"position": v(2501.9, -236.98) * mm});
            skLineSegment(sketch, "E203.MirrorCS", {"start": v(2249.42, -236.98) * mm, "end": v(2474.98, -236.98) * mm});
            skPoint(sketch, "E204.MirrorP", {"position": v(2362.2, -241.3) * mm});
            skPoint(sketch, "E205.MirrorP", {"position": v(2501.9, -245.62) * mm});
            skLineSegment(sketch, "E206.MirrorCS", {"start": v(2249.42, -245.62) * mm, "end": v(2249.42, -368.3) * mm});
            skLineSegment(sketch, "E207.MirrorCS", {"start": v(2474.98, -245.62) * mm, "end": v(2474.98, -368.3) * mm});
            skLineSegment(sketch, "E208.MirrorCS", {"start": v(2249.42, -114.3) * mm, "end": v(2249.42, -236.98) * mm});
            skLineSegment(sketch, "E209.MirrorCS", {"start": v(2474.98, -114.3) * mm, "end": v(2474.98, -236.98) * mm});
            skLineSegment(sketch, "E210.MirrorCS", {"start": v(2235.2, -114.3) * mm, "end": v(2235.2, -368.3) * mm});
            skLineSegment(sketch, "E211.MirrorCS", {"start": v(2489.2, -114.3) * mm, "end": v(2489.2, -368.3) * mm});
            skSolve(sketch);
        }
        {
            var Q0;
            Q0 = qSketchRegion(id + "F13", true);
            extrude(context, id + "F14", {"entities" : qUnion([Q0]), "depth" : 198.37 * mm});
        }
        {
            var Q0;
            Q0=makeQuery(id+"F12.opExtrude","SWEPT_FACE",FACE,{"disambiguationData":[OSD([sQuery(id+"F11.wireOp",EDGE,"E169.top")])]});
            var sketch = newSketch(context, id + "F15", { "sketchPlane" : qUnion([Q0])});
            skLineSegment(sketch, "E212.0", {"start": v(-1615.4, -241.3) * mm, "end": v(2831.5, -241.3) * mm, "construction": true});
            skLineSegment(sketch, "E213.0", {"start": v(0, -413.23) * mm, "end": v(0, 639.03) * mm, "construction": true});
            skPoint(sketch, "E214.orphan", {"position": v(-1320.8, -241.3) * mm});
            skLineSegment(sketch, "E215.0", {"start": v(-1168.4, -689.85) * mm, "end": v(-1168.4, 639.03) * mm, "construction": true});
            skLineSegment(sketch, "E216.0", {"start": v(-1130.3, -355.6) * mm, "end": v(-1130.3, -127) * mm});
            skLineSegment(sketch, "E217.0", {"start": v(-1206.5, -127) * mm, "end": v(-1130.3, -127) * mm});
            skLineSegment(sketch, "E218.0", {"start": v(-1615.4, -171.45) * mm, "end": v(2831.5, -171.45) * mm, "construction": true});
            skLineSegment(sketch, "E219.MirrorCS", {"start": v(-1206.5, -355.6) * mm, "end": v(-1130.3, -355.6) * mm});
            skLineSegment(sketch, "E220.MirrorCS", {"start": v(-1206.5, -355.6) * mm, "end": v(-1206.5, -127) * mm});
            skPoint(sketch, "E221.orphan", {"position": v(-1130.3, 639.03) * mm});
            skPoint(sketch, "E222.orphan", {"position": v(-1206.5, 639.03) * mm});
            skPoint(sketch, "E223.orphan", {"position": v(-1615.4, -127) * mm});
            skPoint(sketch, "E224.orphan", {"position": v(-1615.4, -355.6) * mm});
            skPoint(sketch, "E225.orphan", {"position": v(-1206.5, -689.85) * mm});
            skPoint(sketch, "E226.orphan", {"position": v(-1130.3, -689.85) * mm});
            skCircle(sketch, "E227", {"center": v(-1168.4, -171.45) * mm, "radius": 11.11 * mm});
            skCircle(sketch, "E228.MirrorC", {"center": v(-1168.4, -311.15) * mm, "radius": 11.11 * mm});
            skLineSegment(sketch, "E229.1.0.0", {"start": v(1130.3, -355.6) * mm, "end": v(1130.3, -127) * mm});
            skLineSegment(sketch, "E229.1.0.1", {"start": v(1130.3, -355.6) * mm, "end": v(1206.5, -355.6) * mm});
            skLineSegment(sketch, "E229.1.0.2", {"start": v(1130.3, -127) * mm, "end": v(1206.5, -127) * mm});
            skLineSegment(sketch, "E229.1.0.3", {"start": v(1206.5, -355.6) * mm, "end": v(1206.5, -127) * mm});
            skCircle(sketch, "E229.1.0.4", {"center": v(1168.4, -171.45) * mm, "radius": 11.11 * mm});
            skCircle(sketch, "E229.1.0.5", {"center": v(1168.4, -311.15) * mm, "radius": 11.11 * mm});
            skLineSegment(sketch, "E229.direction1", {"start": v(-1206.5, -355.6) * mm, "end": v(1130.3, -355.6) * mm, "construction": true});
            skLineSegment(sketch, "E230.1.0.1", {"start": v(2578.1, -355.6) * mm, "end": v(2578.1, -127) * mm});
            skLineSegment(sketch, "E230.1.0.2", {"start": v(2654.3, -355.6) * mm, "end": v(2654.3, -127) * mm});
            skCircle(sketch, "E230.1.0.3", {"center": v(2616.2, -311.15) * mm, "radius": 11.11 * mm});
            skCircle(sketch, "E230.1.0.4", {"center": v(2616.2, -171.45) * mm, "radius": 11.11 * mm});
            skLineSegment(sketch, "E230.1.0.5", {"start": v(2578.1, -355.6) * mm, "end": v(2654.3, -355.6) * mm});
            skLineSegment(sketch, "E230.1.0.6", {"start": v(2578.1, -127) * mm, "end": v(2654.3, -127) * mm});
            skLineSegment(sketch, "E230.direction1", {"start": v(1320.8, -241.3) * mm, "end": v(2768.6, -241.3) * mm, "construction": true});
            skSolve(sketch);
        }
        {
            var Q0;
            Q0 = qSketchRegion(id + "F15", true);
            extrude(context, id + "F16", {"entities" : qUnion([Q0]), "operationType" : NewBodyOperationType.ADD, "depth" : 19.05 * mm});
        }
        {
            var Q0;
            Q0=makeQuery(id+"F12.opExtrude","SWEPT_FACE",FACE,{"disambiguationData":[OSD([sQuery(id+"F11.wireOp",EDGE,"E173.MirrorCS")])]});
            var sketch = newSketch(context, id + "F17", { "sketchPlane" : qUnion([Q0])});
            skLineSegment(sketch, "E231", {"start": v(0, -262.73) * mm, "end": v(0, 1224.7) * mm, "construction": true});
            skLineSegment(sketch, "E232.0", {"start": v(-1320.8, 0) * mm, "end": v(1320.8, 0) * mm, "construction": true});
            skLineSegment(sketch, "E233.0", {"start": v(-1320.8, 231.9) * mm, "end": v(1320.8, 231.9) * mm, "construction": true});
            skLineSegment(sketch, "E234.0", {"start": v(-1187.45, -262.73) * mm, "end": v(-1187.45, 1224.7) * mm, "construction": true});
            skLineSegment(sketch, "E235.0", {"start": v(-1320.8, 333.5) * mm, "end": v(1320.8, 333.5) * mm, "construction": true});
            skLineSegment(sketch, "E236.bottom", {"start": v(-1289.05, 435.1) * mm, "end": v(-1085.85, 435.1) * mm});
            skLineSegment(sketch, "E236.top", {"start": v(-1289.05, 231.9) * mm, "end": v(-1085.85, 231.9) * mm});
            skLineSegment(sketch, "E236.left", {"start": v(-1289.05, 435.1) * mm, "end": v(-1289.05, 424.05) * mm});
            skLineSegment(sketch, "E236.right", {"start": v(-1085.85, 435.1) * mm, "end": v(-1085.85, 424.05) * mm});
            skPoint(sketch, "E236.middle", {"position": v(-1187.45, 333.5) * mm});
            skLineSegment(sketch, "E237.0", {"start": v(-1289.05, 424.05) * mm, "end": v(-1197.36, 424.05) * mm});
            skLineSegment(sketch, "E238.MirrorCS", {"start": v(-1289.05, 242.95) * mm, "end": v(-1197.36, 242.95) * mm});
            skLineSegment(sketch, "E239.0", {"start": v(-1183.9, 249.3) * mm, "end": v(-1183.9, 417.7) * mm});
            skLineSegment(sketch, "E240.MirrorCS", {"start": v(-1191, 249.3) * mm, "end": v(-1191, 417.7) * mm});
            skLineSegment(sketch, "E241", {"start": v(-1177.54, 424.05) * mm, "end": v(-1085.85, 424.05) * mm});
            skLineSegment(sketch, "E242", {"start": v(-1177.54, 242.95) * mm, "end": v(-1085.85, 242.95) * mm});
            skPoint(sketch, "E243.newPointB", {"position": v(-1191, 1224.7) * mm});
            skArc(sketch, "E243.filletArc", {"start": v(-1191, 417.7) * mm, "mid": v(-1192.87, 422.2) * mm, "end": v(-1197.36, 424.05) * mm});
            skPoint(sketch, "E244.newPointA", {"position": v(-1191, -262.73) * mm});
            skArc(sketch, "E244.filletArc", {"start": v(-1197.36, 242.95) * mm, "mid": v(-1192.87, 244.81) * mm, "end": v(-1191, 249.3) * mm});
            skPoint(sketch, "E245.newPointA", {"position": v(-1183.9, -262.73) * mm});
            skArc(sketch, "E245.filletArc", {"start": v(-1183.9, 249.3) * mm, "mid": v(-1182.03, 244.81) * mm, "end": v(-1177.54, 242.95) * mm});
            skPoint(sketch, "E246.newPointB", {"position": v(-1183.9, 1224.7) * mm});
            skArc(sketch, "E246.filletArc", {"start": v(-1177.54, 424.05) * mm, "mid": v(-1182.03, 422.2) * mm, "end": v(-1183.9, 417.7) * mm});
            skLineSegment(sketch, "E247.trimOffspring", {"start": v(-1289.05, 242.95) * mm, "end": v(-1289.05, 231.9) * mm});
            skLineSegment(sketch, "E248.trimOffspring", {"start": v(-1085.85, 242.95) * mm, "end": v(-1085.85, 231.9) * mm});
            skArc(sketch, "E249.MirrorCS", {"start": v(1177.54, 424.05) * mm, "mid": v(1182.03, 422.2) * mm, "end": v(1183.9, 417.7) * mm});
            skArc(sketch, "E250.MirrorCS", {"start": v(1183.9, 249.3) * mm, "mid": v(1182.03, 244.81) * mm, "end": v(1177.54, 242.95) * mm});
            skArc(sketch, "E251.MirrorCS", {"start": v(1197.36, 242.95) * mm, "mid": v(1192.87, 244.81) * mm, "end": v(1191, 249.3) * mm});
            skArc(sketch, "E252.MirrorCS", {"start": v(1191, 417.7) * mm, "mid": v(1192.87, 422.2) * mm, "end": v(1197.36, 424.05) * mm});
            skLineSegment(sketch, "E253.MirrorCS", {"start": v(1085.85, 242.95) * mm, "end": v(1085.85, 231.9) * mm});
            skLineSegment(sketch, "E254.MirrorCS", {"start": v(1183.9, 249.3) * mm, "end": v(1183.9, 417.7) * mm});
            skLineSegment(sketch, "E255.MirrorCS", {"start": v(1289.05, 242.95) * mm, "end": v(1289.05, 231.9) * mm});
            skLineSegment(sketch, "E256.MirrorCS", {"start": v(1085.85, 435.1) * mm, "end": v(1085.85, 424.05) * mm});
            skLineSegment(sketch, "E257.MirrorCS", {"start": v(1289.05, 435.1) * mm, "end": v(1289.05, 424.05) * mm});
            skLineSegment(sketch, "E258.MirrorCS", {"start": v(1289.05, 242.95) * mm, "end": v(1197.36, 242.95) * mm});
            skLineSegment(sketch, "E259.MirrorCS", {"start": v(1289.05, 424.05) * mm, "end": v(1197.36, 424.05) * mm});
            skLineSegment(sketch, "E260.MirrorCS", {"start": v(1289.05, 435.1) * mm, "end": v(1085.85, 435.1) * mm});
            skLineSegment(sketch, "E261.MirrorCS", {"start": v(1177.54, 424.05) * mm, "end": v(1085.85, 424.05) * mm});
            skLineSegment(sketch, "E262.MirrorCS", {"start": v(1289.05, 231.9) * mm, "end": v(1085.85, 231.9) * mm});
            skLineSegment(sketch, "E263.MirrorCS", {"start": v(1177.54, 242.95) * mm, "end": v(1085.85, 242.95) * mm});
            skLineSegment(sketch, "E264.MirrorCS", {"start": v(1191, 249.3) * mm, "end": v(1191, 417.7) * mm});
            skPoint(sketch, "E265.MirrorP", {"position": v(1187.45, 333.5) * mm});
            skSolve(sketch);
        }
        {
            var Q0;
            Q0 = qSketchRegion(id + "F17", true);
            extrude(context, id + "F18", {"entities" : qUnion([Q0]), "depth" : 401.57 * mm});
        }
        {
            var Q0;
            Q0=makeQuery(id+"F18.opExtrude","SWEPT_FACE",FACE,{"disambiguationData":[OSD([sQuery(id+"F17.wireOp",EDGE,"E236.bottom")])]});
            var sketch = newSketch(context, id + "F19", { "sketchPlane" : qUnion([Q0])});
            skLineSegment(sketch, "E266.bottom", {"start": v(-1289.05, -649.22) * mm, "end": v(-1278, -649.22) * mm});
            skLineSegment(sketch, "E266.top", {"start": v(-1289.05, -446.02) * mm, "end": v(-1278, -446.02) * mm});
            skLineSegment(sketch, "E266.left", {"start": v(-1289.05, -649.22) * mm, "end": v(-1289.05, -446.02) * mm});
            skLineSegment(sketch, "E266.right", {"start": v(-1085.85, -649.22) * mm, "end": v(-1085.85, -446.02) * mm});
            skLineSegment(sketch, "E267", {"start": v(-1187.45, -446.02) * mm, "end": v(-1187.45, -700.9) * mm, "construction": true});
            skLineSegment(sketch, "E268", {"start": v(-1289.05, -547.62) * mm, "end": v(-1023.84, -547.62) * mm, "construction": true});
            skLineSegment(sketch, "E269.0", {"start": v(-1278, -649.22) * mm, "end": v(-1278, -557.53) * mm});
            skLineSegment(sketch, "E270.MirrorCS", {"start": v(-1096.9, -649.22) * mm, "end": v(-1096.9, -557.53) * mm});
            skLineSegment(sketch, "E271.0", {"start": v(-1271.65, -551.18) * mm, "end": v(-1103.25, -551.18) * mm});
            skLineSegment(sketch, "E272.MirrorCS", {"start": v(-1271.65, -544.07) * mm, "end": v(-1103.25, -544.07) * mm});
            skPoint(sketch, "E273.orphan", {"position": v(-1023.84, -551.18) * mm});
            skPoint(sketch, "E274.orphan", {"position": v(-1023.84, -544.07) * mm});
            skLineSegment(sketch, "E275.trimOffspring", {"start": v(-1096.9, -537.72) * mm, "end": v(-1096.9, -446.02) * mm});
            skPoint(sketch, "E276.orphan", {"position": v(-1289.05, -544.07) * mm});
            skLineSegment(sketch, "E277.trimOffspring", {"start": v(-1278, -537.72) * mm, "end": v(-1278, -446.02) * mm});
            skPoint(sketch, "E278.orphan", {"position": v(-1289.05, -551.18) * mm});
            skLineSegment(sketch, "E279.trimOffspring", {"start": v(-1096.9, -446.02) * mm, "end": v(-1085.85, -446.02) * mm});
            skLineSegment(sketch, "E280.trimOffspring", {"start": v(-1096.9, -649.22) * mm, "end": v(-1085.85, -649.22) * mm});
            skPoint(sketch, "E281.visualSharp", {"position": v(-1278, -544.07) * mm});
            skArc(sketch, "E281.filletArc", {"start": v(-1278, -537.72) * mm, "mid": v(-1276.14, -542.2) * mm, "end": v(-1271.65, -544.07) * mm});
            skPoint(sketch, "E282.visualSharp", {"position": v(-1278, -551.18) * mm});
            skArc(sketch, "E282.filletArc", {"start": v(-1271.65, -551.18) * mm, "mid": v(-1276.14, -553.04) * mm, "end": v(-1278, -557.53) * mm});
            skPoint(sketch, "E283.visualSharp", {"position": v(-1096.9, -551.18) * mm});
            skArc(sketch, "E283.filletArc", {"start": v(-1096.9, -557.53) * mm, "mid": v(-1098.76, -553.04) * mm, "end": v(-1103.25, -551.18) * mm});
            skPoint(sketch, "E284.visualSharp", {"position": v(-1096.9, -544.07) * mm});
            skArc(sketch, "E284.filletArc", {"start": v(-1103.25, -544.07) * mm, "mid": v(-1098.76, -542.2) * mm, "end": v(-1096.9, -537.72) * mm});
            skArc(sketch, "E285.MirrorCS", {"start": v(1271.65, -551.18) * mm, "mid": v(1276.14, -553.04) * mm, "end": v(1278, -557.53) * mm});
            skArc(sketch, "E286.MirrorCS", {"start": v(1278, -537.72) * mm, "mid": v(1276.14, -542.2) * mm, "end": v(1271.65, -544.07) * mm});
            skArc(sketch, "E287.MirrorCS", {"start": v(1096.9, -557.53) * mm, "mid": v(1098.76, -553.04) * mm, "end": v(1103.25, -551.18) * mm});
            skArc(sketch, "E288.MirrorCS", {"start": v(1103.25, -544.07) * mm, "mid": v(1098.76, -542.2) * mm, "end": v(1096.9, -537.72) * mm});
            skLineSegment(sketch, "E289.MirrorCS", {"start": v(1289.05, -547.62) * mm, "end": v(1023.84, -547.62) * mm, "construction": true});
            skLineSegment(sketch, "E290.MirrorCS", {"start": v(1096.9, -649.22) * mm, "end": v(1085.85, -649.22) * mm});
            skLineSegment(sketch, "E291.MirrorCS", {"start": v(1289.05, -649.22) * mm, "end": v(1278, -649.22) * mm});
            skLineSegment(sketch, "E292.MirrorCS", {"start": v(1289.05, -446.02) * mm, "end": v(1278, -446.02) * mm});
            skPoint(sketch, "E293.MirrorP", {"position": v(1096.9, -551.18) * mm});
            skLineSegment(sketch, "E294.MirrorCS", {"start": v(1096.9, -446.02) * mm, "end": v(1085.85, -446.02) * mm});
            skPoint(sketch, "E295.MirrorP", {"position": v(1289.05, -544.07) * mm});
            skPoint(sketch, "E296.MirrorP", {"position": v(1278, -551.18) * mm});
            skLineSegment(sketch, "E297.MirrorCS", {"start": v(1271.65, -551.18) * mm, "end": v(1103.25, -551.18) * mm});
            skLineSegment(sketch, "E298.MirrorCS", {"start": v(1289.05, -649.22) * mm, "end": v(1289.05, -446.02) * mm});
            skPoint(sketch, "E299.MirrorP", {"position": v(1289.05, -551.18) * mm});
            skLineSegment(sketch, "E300.MirrorCS", {"start": v(1085.85, -649.22) * mm, "end": v(1085.85, -446.02) * mm});
            skPoint(sketch, "E301.MirrorP", {"position": v(1278, -544.07) * mm});
            skLineSegment(sketch, "E302.MirrorCS", {"start": v(1096.9, -649.22) * mm, "end": v(1096.9, -557.53) * mm});
            skLineSegment(sketch, "E303.MirrorCS", {"start": v(1278, -537.72) * mm, "end": v(1278, -446.02) * mm});
            skLineSegment(sketch, "E304.MirrorCS", {"start": v(1278, -649.22) * mm, "end": v(1278, -557.53) * mm});
            skLineSegment(sketch, "E305.MirrorCS", {"start": v(1271.65, -544.07) * mm, "end": v(1103.25, -544.07) * mm});
            skPoint(sketch, "E306.MirrorP", {"position": v(1096.9, -544.07) * mm});
            skPoint(sketch, "E307.MirrorP", {"position": v(1023.84, -544.07) * mm});
            skLineSegment(sketch, "E308.MirrorCS", {"start": v(1096.9, -537.72) * mm, "end": v(1096.9, -446.02) * mm});
            skLineSegment(sketch, "E309.MirrorCS", {"start": v(1187.45, -446.02) * mm, "end": v(1187.45, -700.9) * mm, "construction": true});
            skPoint(sketch, "E310.MirrorP", {"position": v(1023.84, -551.18) * mm});
            skSolve(sketch);
        }
        {
            var Q0;
            Q0 = qSketchRegion(id + "F19", true);
            extrude(context, id + "F20", {"entities" : qUnion([Q0]), "depth" : 292.1 * mm});
        }
        {
            var Q0;
            Q0=makeQuery(id+"F20.opExtrude","CAP_FACE",FACE,{"disambiguationData":[OSD([sQuery(id+"F19.wireOp",EDGE,"E266.bottom"),sQuery(id+"F19.wireOp",EDGE,"E266.top"),sQuery(id+"F19.wireOp",EDGE,"E266.left"),sQuery(id+"F19.wireOp",EDGE,"E266.right"),sQuery(id+"F19.wireOp",EDGE,"E269.0"),sQuery(id+"F19.wireOp",EDGE,"E270.MirrorCS"),sQuery(id+"F19.wireOp",EDGE,"E271.0"),sQuery(id+"F19.wireOp",EDGE,"E272.MirrorCS"),sQuery(id+"F19.wireOp",EDGE,"E275.trimOffspring"),sQuery(id+"F19.wireOp",EDGE,"E277.trimOffspring"),sQuery(id+"F19.wireOp",EDGE,"E279.trimOffspring"),sQuery(id+"F19.wireOp",EDGE,"E280.trimOffspring"),sQuery(id+"F19.wireOp",EDGE,"E281.filletArc"),sQuery(id+"F19.wireOp",EDGE,"E282.filletArc"),sQuery(id+"F19.wireOp",EDGE,"E283.filletArc"),sQuery(id+"F19.wireOp",EDGE,"E284.filletArc")])],"isStart":false});
            var sketch = newSketch(context, id + "F21", { "sketchPlane" : qUnion([Q0])});
            skLineSegment(sketch, "E311.0", {"start": v(-1289.05, -649.22) * mm, "end": v(-1289.05, -446.02) * mm, "construction": true});
            skLineSegment(sketch, "E312.0", {"start": v(-1085.85, -649.22) * mm, "end": v(-1085.85, -446.02) * mm, "construction": true});
            skLineSegment(sketch, "E313", {"start": v(-1289.05, -547.62) * mm, "end": v(-1085.85, -547.62) * mm, "construction": true});
            skLineSegment(sketch, "E314.bottom", {"start": v(-1301.75, -433.32) * mm, "end": v(-1073.15, -433.32) * mm});
            skLineSegment(sketch, "E314.top", {"start": v(-1301.75, -661.92) * mm, "end": v(-1073.15, -661.92) * mm});
            skLineSegment(sketch, "E314.left", {"start": v(-1301.75, -433.32) * mm, "end": v(-1301.75, -661.92) * mm});
            skLineSegment(sketch, "E314.right", {"start": v(-1073.15, -433.32) * mm, "end": v(-1073.15, -661.92) * mm});
            skPoint(sketch, "E314.middle", {"position": v(-1187.45, -547.62) * mm});
            skLineSegment(sketch, "E315", {"start": v(-1187.45, -433.32) * mm, "end": v(-1187.45, -661.92) * mm, "construction": true});
            skLineSegment(sketch, "E316.0", {"start": v(-1289.05, -477.77) * mm, "end": v(-1085.85, -477.77) * mm, "construction": true});
            skCircle(sketch, "E317", {"center": v(-1187.45, -477.77) * mm, "radius": 11.11 * mm});
            skCircle(sketch, "E318.MirrorC", {"center": v(-1187.45, -617.47) * mm, "radius": 11.11 * mm});
            skCircle(sketch, "E319.MirrorC", {"center": v(1187.45, -617.47) * mm, "radius": 11.11 * mm});
            skCircle(sketch, "E320.MirrorC", {"center": v(1187.45, -477.77) * mm, "radius": 11.11 * mm});
            skLineSegment(sketch, "E321.MirrorCS", {"start": v(1289.05, -477.77) * mm, "end": v(1085.85, -477.77) * mm, "construction": true});
            skLineSegment(sketch, "E322.MirrorCS", {"start": v(1289.05, -547.62) * mm, "end": v(1085.85, -547.62) * mm, "construction": true});
            skLineSegment(sketch, "E323.MirrorCS", {"start": v(1289.05, -649.22) * mm, "end": v(1289.05, -446.02) * mm, "construction": true});
            skLineSegment(sketch, "E324.MirrorCS", {"start": v(1187.45, -433.32) * mm, "end": v(1187.45, -661.92) * mm, "construction": true});
            skPoint(sketch, "E325.MirrorP", {"position": v(1187.45, -547.62) * mm});
            skLineSegment(sketch, "E326.MirrorCS", {"start": v(1073.15, -433.32) * mm, "end": v(1073.15, -661.92) * mm});
            skLineSegment(sketch, "E327.MirrorCS", {"start": v(1301.75, -661.92) * mm, "end": v(1073.15, -661.92) * mm});
            skLineSegment(sketch, "E328.MirrorCS", {"start": v(1301.75, -433.32) * mm, "end": v(1073.15, -433.32) * mm});
            skLineSegment(sketch, "E329.MirrorCS", {"start": v(1085.85, -649.22) * mm, "end": v(1085.85, -446.02) * mm, "construction": true});
            skLineSegment(sketch, "E330.MirrorCS", {"start": v(1301.75, -433.32) * mm, "end": v(1301.75, -661.92) * mm});
            skSolve(sketch);
        }
        {
            var Q0;
            Q0 = qSketchRegion(id + "F21", true);
            extrude(context, id + "F22", {"entities" : qUnion([Q0]), "depth" : 19.05 * mm});
        }
        {
            var Q0;
            Q0=makeQuery(id+"F20.opExtrude","SWEPT_FACE",FACE,{"disambiguationData":[OSD([sQuery(id+"F19.wireOp",EDGE,"E266.right")])]});
            var sketch = newSketch(context, id + "F23", { "sketchPlane" : qUnion([Q0])});
            skLineSegment(sketch, "E331.0.0", {"start": v(-649.22, 435.1) * mm, "end": v(-446.02, 435.1) * mm, "construction": true});
            skLineSegment(sketch, "E331.0.1", {"start": v(-446.02, 435.1) * mm, "end": v(-446.02, 727.2) * mm, "construction": true});
            skLineSegment(sketch, "E331.0.2", {"start": v(-446.02, 727.2) * mm, "end": v(-649.22, 727.2) * mm, "construction": true});
            skLineSegment(sketch, "E331.0.3", {"start": v(-649.22, 727.2) * mm, "end": v(-649.22, 435.1) * mm, "construction": true});
            skLineSegment(sketch, "E332.0", {"start": v(-446.02, 574.8) * mm, "end": v(-649.22, 574.8) * mm, "construction": true});
            skLineSegment(sketch, "E333", {"start": v(-547.62, 574.8) * mm, "end": v(-547.62, 602) * mm, "construction": true});
            skCircle(sketch, "E334", {"center": v(-547.62, 574.8) * mm, "radius": 44.45 * mm});
            skCircle(sketch, "E335.0", {"center": v(-547.62, 574.8) * mm, "radius": 38.96 * mm});
            skSolve(sketch);
        }
        {
            var Q0;
            Q0 = qSketchRegion(id + "F23", true);
            extrude(context, id + "F24", {"entities" : qUnion([Q0]), "depth" : 2171.7 * mm});
        }
    });
